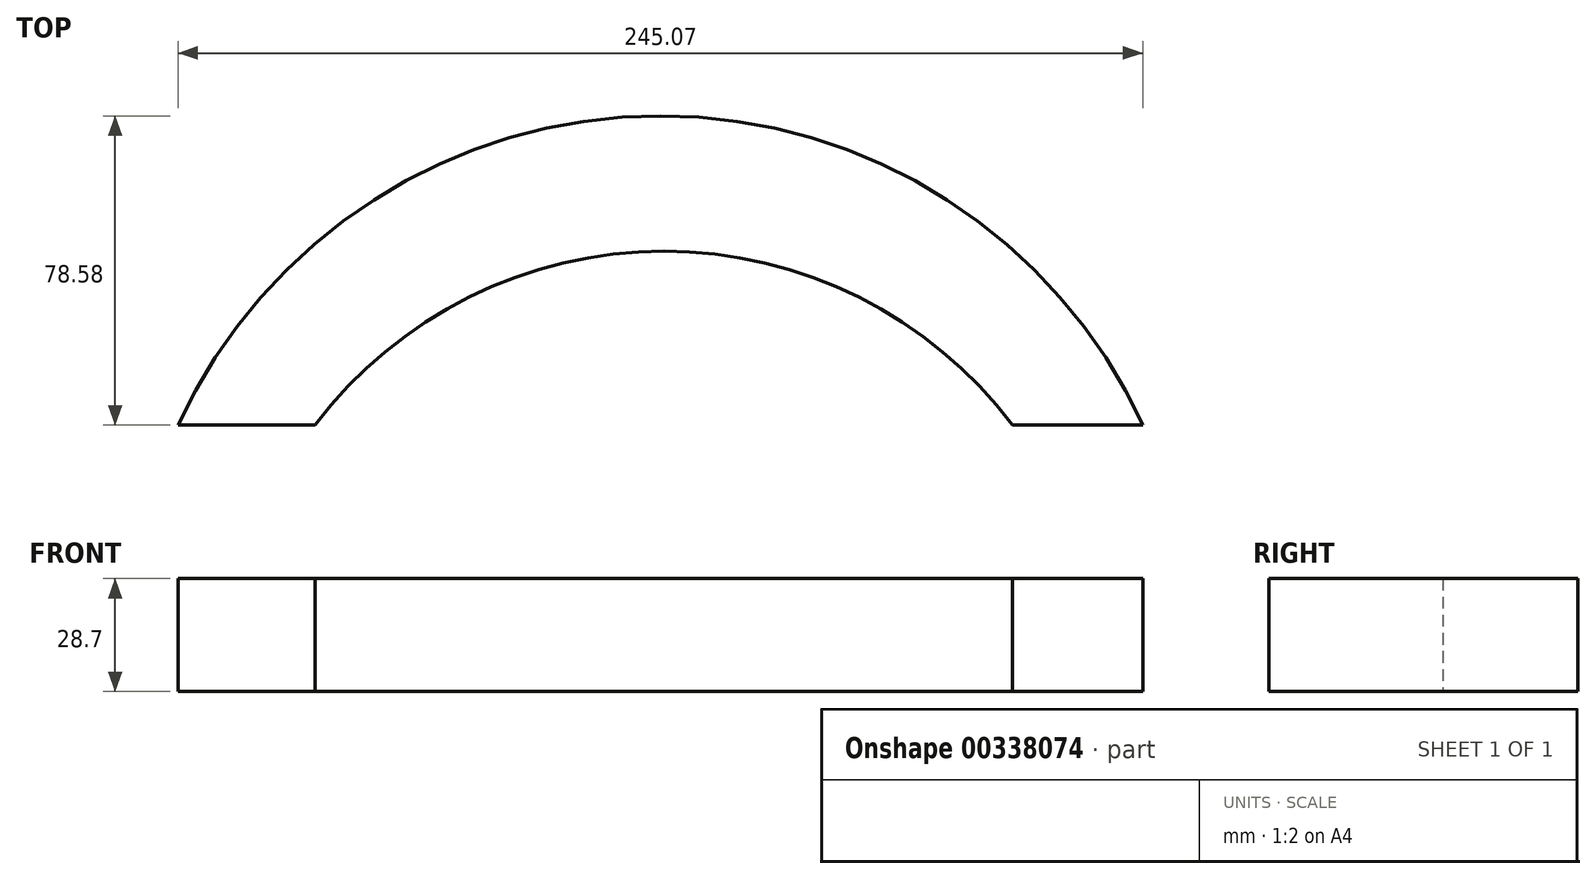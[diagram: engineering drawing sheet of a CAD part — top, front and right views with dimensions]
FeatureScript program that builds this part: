
annotation { "Feature Type Name" : "Feature", "Feature Type Description" : "" }
export const myFeature = defineFeature(function(context is Context, id is Id, definition is map)
    precondition{}
    {
        {
            var Q0;
            Q0=qCreatedBy(makeId("Top.planeOp"),FACE);
            var sketch = newSketch(context, id + "F0", { "sketchPlane" : qUnion([Q0])});
            skPoint(sketch, "E0", {"position": v(-121.51, 0) * mm});
            skPoint(sketch, "E1", {"position": v(0, 0) * mm});
            skPoint(sketch, "E2", {"position": v(123.56, 0) * mm});
            skArc(sketch, "E3", {"start": v(123.56, 0) * mm, "mid": v(1.03, 78.58) * mm, "end": v(-121.51, 0) * mm});
            skLineSegment(sketch, "E4", {"start": v(-121.51, 0) * mm, "end": v(-86.7, 0) * mm});
            skLineSegment(sketch, "E5", {"start": v(90.5, 0) * mm, "end": v(123.56, 0) * mm});
            skArc(sketch, "E6", {"start": v(90.5, 0) * mm, "mid": v(1.9, 44.2) * mm, "end": v(-86.7, 0) * mm});
            skSolve(sketch);
        }
        {
            var Q0;
            Q0 = qSketchRegion(id + "F0", true);
            extrude(context, id + "F1", {"entities" : qUnion([Q0]), "depth" : 28.7 * mm});
        }
    });
